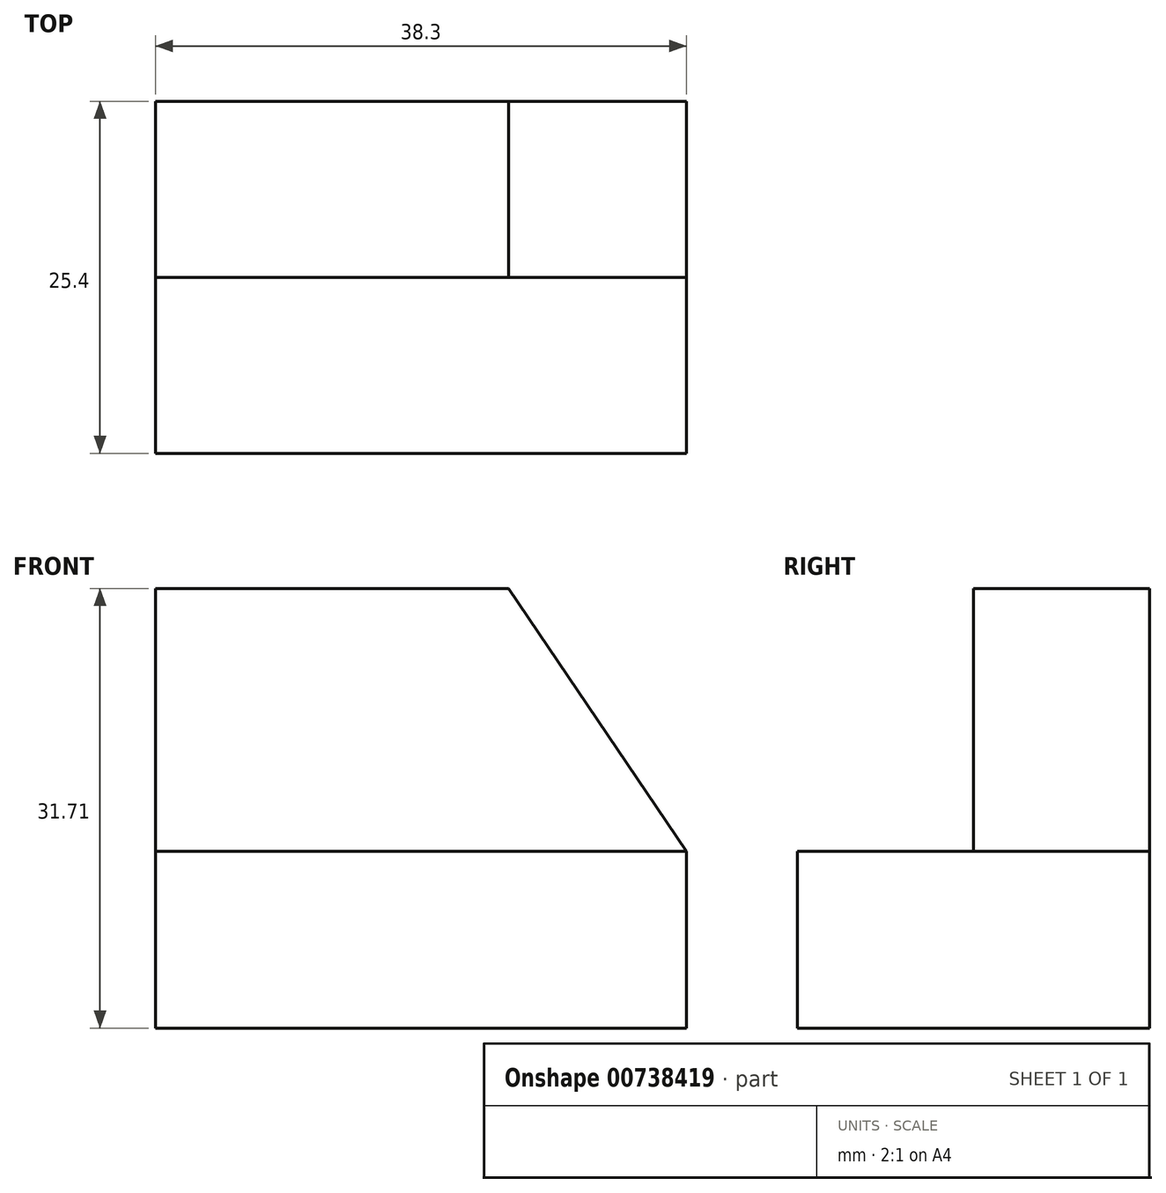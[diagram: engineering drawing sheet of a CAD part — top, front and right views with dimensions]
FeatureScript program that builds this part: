
annotation { "Feature Type Name" : "Feature", "Feature Type Description" : "" }
export const myFeature = defineFeature(function(context is Context, id is Id, definition is map)
    precondition{}
    {
        {
            var Q0;
            Q0=qCreatedBy(makeId("Front.planeOp"),FACE);
            var sketch = newSketch(context, id + "F0", { "sketchPlane" : qUnion([Q0])});
            skLineSegment(sketch, "E0", {"start": v(0, 0) * mm, "end": v(0, 31.71) * mm});
            skLineSegment(sketch, "E1", {"start": v(0, 31.71) * mm, "end": v(38.3, 31.71) * mm});
            skLineSegment(sketch, "E2", {"start": v(38.3, 31.71) * mm, "end": v(38.3, 0) * mm});
            skLineSegment(sketch, "E3", {"start": v(38.3, 0) * mm, "end": v(0, 0) * mm});
            skSolve(sketch);
        }
        {
            var Q0;
            Q0 = qSketchRegion(id + "F0", true);
            extrude(context, id + "F1", {"entities" : qUnion([Q0]), "depth" : 25.4 * mm, "offsetDistance" : 25.4 * mm});
        }
        {
            var Q0;
            Q0=makeQuery(id+"F1.opExtrude","CAP_FACE",FACE,{"disambiguationData":[OSD([sQuery(id+"F0.wireOp",EDGE,"E0"),sQuery(id+"F0.wireOp",EDGE,"E1"),sQuery(id+"F0.wireOp",EDGE,"E2"),sQuery(id+"F0.wireOp",EDGE,"E3")])],"isStart":false});
            var sketch = newSketch(context, id + "F2", { "sketchPlane" : qUnion([Q0])});
            skLineSegment(sketch, "E4", {"start": v(0, 0) * mm, "end": v(0, 12.74) * mm});
            skLineSegment(sketch, "E5", {"start": v(0, 12.74) * mm, "end": v(38.3, 12.74) * mm});
            skSolve(sketch);
        }
        {
            var Q0;
            {var subQ0=sQuery(id+"F2.wireOp",EDGE,"E5");Q0=makeQuery(id+"F2.imprint","IMPRINT",FACE,{"disambiguationData":[TD([[makeQuery(id+"F2.imprint","IMPRINT",EDGE,{"derivedFrom":subQ0}),1.0]])]});}
            extrude(context, id + "F3", {"entities" : qUnion([Q0]), "operationType" : NewBodyOperationType.REMOVE, "oppositeDirection" : true, "depth" : 12.7 * mm, "offsetDistance" : 25.4 * mm});
        }
        {
            var Q0;
            Q0=makeQuery(id+"F3.boolean.opBoolean","COPY",FACE,{"derivedFrom":makeQuery(id+"F3.opExtrude","CAP_FACE",FACE,{"disambiguationData":[OSD([sQuery(id+"F0.wireOp",EDGE,"E0"),sQuery(id+"F0.wireOp",EDGE,"E1"),sQuery(id+"F0.wireOp",EDGE,"E2"),sQuery(id+"F2.wireOp",EDGE,"E5")])],"isStart":false})});
            var sketch = newSketch(context, id + "F4", { "sketchPlane" : qUnion([Q0])});
            skLineSegment(sketch, "E6", {"start": v(0, 31.71) * mm, "end": v(25.47, 31.71) * mm});
            skLineSegment(sketch, "E7", {"start": v(25.47, 31.71) * mm, "end": v(38.3, 12.74) * mm});
            skSolve(sketch);
        }
        {
            var Q0;
            {var subQ0=sQuery(id+"F4.wireOp",EDGE,"E7");Q0=makeQuery(id+"F4.imprint","IMPRINT",FACE,{"disambiguationData":[TD([[makeQuery(id+"F4.imprint","IMPRINT",EDGE,{"derivedFrom":subQ0}),1.0]])]});}
            extrude(context, id + "F5", {"entities" : qUnion([Q0]), "operationType" : NewBodyOperationType.REMOVE, "endBound" : BoundingType.THROUGH_ALL, "oppositeDirection" : true, "depth" : 25.4 * mm, "offsetDistance" : 25.4 * mm});
        }
    });
